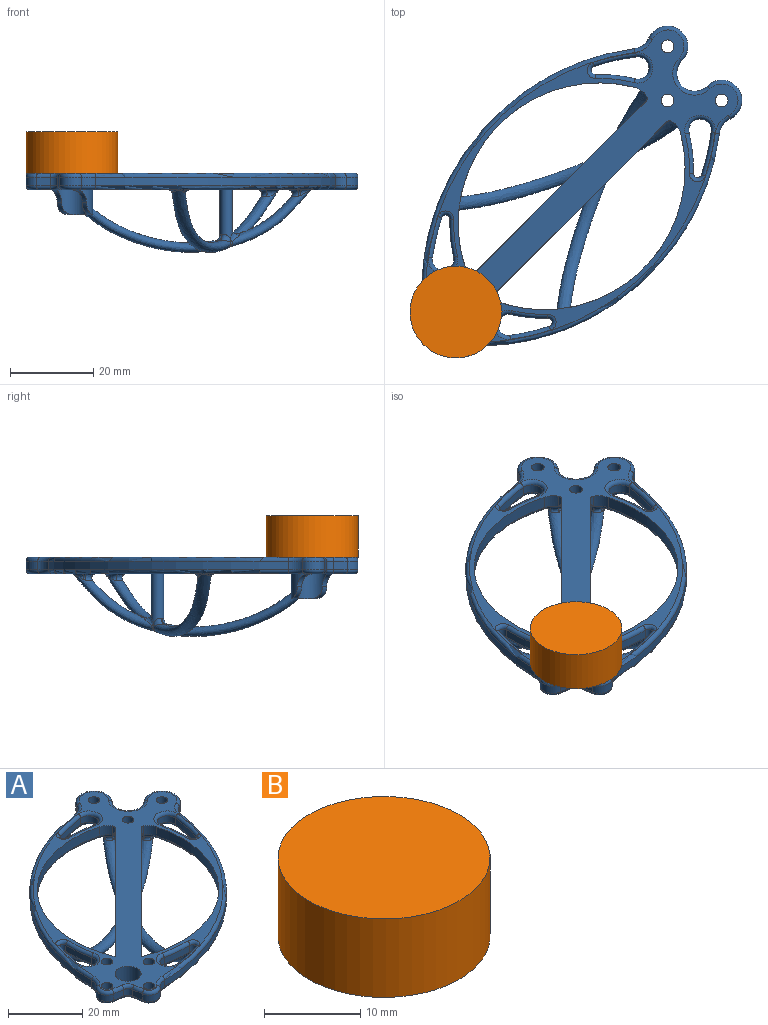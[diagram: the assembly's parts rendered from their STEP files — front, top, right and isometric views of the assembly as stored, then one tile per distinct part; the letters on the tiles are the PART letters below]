
ASSEMBLY  parts=2 mates=1
PART A: 190 faces, bbox 82.3x82.3x19.1 mm
  f0: plane 35.32x35.1mm, normal (0,0,-1), area 158.4mm2, adj f44,f45,f46,f47,f56,f72,f73,f75
  f1: bspline ~3.8x3.75mm, area 3mm2, adj f3,f5,f16,f170
  f2: bspline ~5.97x4.34mm, area 4.7mm2, adj f4,f5,f17,f173
  f3: bspline ~21.16x13.88mm, area 178.6mm2, adj f1,f7,f15,f16,f142,f143,f144,f145
  f4: bspline ~40.35x14.86mm, area 345.9mm2, adj f2,f6,f14,f17,f124,f125,f126,f127
  f5: bspline ~60.31x25.47mm, area 536.7mm2, adj f1,f2,f6,f7,f14,f15,f16,f17
  f6: bspline ~3.46x3.45mm, area 3.1mm2, adj f4,f5,f14,f176
  f7: bspline ~6.58x4.81mm, area 6.2mm2, adj f3,f5,f15,f179
  f8: cylinder r=4.5mm len=3.73mm, axis (0,0,1), area 11mm2, adj f9,f13,f57,f110,f157,f158
  f9: cylinder r=33.94mm len=49.02mm, axis (0,0,1), area 230.7mm2, adj f8,f10,f57,f112,f149,f151,f164
  f10: cylinder r=4.5mm len=2.03mm, axis (0,0,1), area 0.1mm2, adj f9,f11,f114,f152
  f11: cylinder r=33.94mm len=49.02mm, axis (0,0,1), area 230.7mm2, adj f10,f12,f57,f115,f150,f153,f159
  f12: cylinder r=4.5mm len=3.73mm, axis (0,0,1), area 11mm2, adj f11,f13,f57,f113,f154,f155
  f13: cylinder r=4.5mm len=3.84mm, axis (0,0,1), area 0.3mm2, adj f8,f12,f111,f156
  f14: bspline ~2.25x2.25mm, area 1.8mm2, adj f4,f5,f6,f17
  f15: bspline ~3x2.99mm, area 2.5mm2, adj f3,f5,f7,f16
  f16: bspline ~2.93x2.91mm, area 2.5mm2, adj f1,f3,f5,f15
  f17: bspline ~2.22x2.22mm, area 1.7mm2, adj f2,f4,f5,f14
  f18: plane 70.48x70.39mm, normal (0,0,-1), area 284.4mm2, adj f50,f51,f52,f72,f74,f76,f78,f80
  f19: cylinder r=2.59mm len=5.17mm, axis (0,0,1), area 19.1mm2, adj f20,f48,f86,f102
  f20: cylinder r=35.94mm len=9.11mm, axis (0,0,1), area 19.3mm2, adj f19,f21,f88,f104
  f21: cylinder r=1mm len=2.1mm, axis (0,0,1), area 6mm2, adj f20,f48,f89,f105
  f22: cylinder r=2.56mm len=5.12mm, axis (0,0,1), area 18.9mm2, adj f23,f49,f92,f106
  f23: cylinder r=56.93mm len=9.47mm, axis (0,0,1), area 20.4mm2, adj f22,f24,f90,f108
  f24: cylinder r=1mm len=2.1mm, axis (0,0,1), area 6mm2, adj f23,f49,f91,f109
  f25: cylinder r=35.97mm len=9.55mm, axis (0,0,1), area 20.2mm2, adj f26,f53,f94,f117
  f26: cylinder r=2.69mm len=5.38mm, axis (0,0,1), area 19.8mm2, adj f25,f27,f96,f116
  f27: cylinder r=56.93mm len=10.18mm, axis (0,0,1), area 22mm2, adj f26,f53,f97,f118
  f28: cylinder r=2.72mm len=5.43mm, axis (0,0,1), area 20mm2, adj f29,f54,f99,f120
  f29: cylinder r=35.94mm len=9.74mm, axis (0,0,1), area 20.6mm2, adj f28,f30,f101,f122
  f30: cylinder r=1mm len=2.1mm, axis (0,0,1), area 6mm2, adj f29,f54,f100,f123
  f31: cylinder r=4.5mm len=3.49mm, axis (0,0,1), area 9.5mm2, adj f32,f55,f59,f82
  f32: cylinder r=58.96mm len=57.62mm, axis (0,0,1), area 176.3mm2, adj f31,f33,f58,f84
  f33: cylinder r=4.5mm len=3.44mm, axis (0,0,1), area 8.3mm2, adj f32,f34,f60,f85
  f34: cylinder r=3mm len=5.31mm, axis (0,0,1), area 14.6mm2, adj f33,f35,f62,f83
  f35: plane 3.28x2.1mm, normal (-0.99,-0.14,0), area 7mm2, adj f34,f36,f64,f81
  f36: cylinder r=2mm len=2.1mm, axis (0,0,1), area 5.4mm2, adj f35,f37,f66,f79
  f37: plane 3.28x2.1mm, normal (-0.14,-0.99,0), area 7mm2, adj f36,f38,f68,f77
  f38: cylinder r=3mm len=5.31mm, axis (0,0,1), area 14.6mm2, adj f37,f39,f70,f75
  f39: cylinder r=4.5mm len=3.44mm, axis (0,0,1), area 8.3mm2, adj f38,f40,f71,f73
  f40: cylinder r=58.96mm len=57.62mm, axis (0,0,1), area 176.3mm2, adj f39,f41,f69,f72
  f41: cylinder r=4.5mm len=3.49mm, axis (0,0,1), area 9.5mm2, adj f40,f42,f67,f74
  f42: cylinder r=4.91mm len=9.37mm, axis (0,0,1), area 36mm2, adj f41,f43,f65,f76
  f43: cylinder r=4.28mm len=7.31mm, axis (0,0,1), area 28.3mm2, adj f42,f55,f63,f78
  f44: cylinder r=1.55mm len=4mm, axis (0,0,1), area 39mm2, adj f0,f57
  f45: cylinder r=1.55mm len=4mm, axis (0,0,1), area 39mm2, adj f0,f57
  f46: cylinder r=1.55mm len=4mm, axis (0,0,1), area 39mm2, adj f0,f57
  f47: cylinder r=3.5mm len=10mm, axis (0,0,1), area 153.9mm2, adj f0,f57,f185,f186,f187,f188,f189
  f48: cylinder r=56.96mm len=9.66mm, axis (0,0,1), area 20.9mm2, adj f19,f21,f87,f103
  f49: cylinder r=35.97mm len=8.93mm, axis (0,0,1), area 18.9mm2, adj f22,f24,f93,f107
  f50: cylinder r=1.55mm len=4mm, axis (0,0,1), area 39mm2, adj f18,f57
  f51: cylinder r=1.55mm len=4mm, axis (0,0,1), area 39mm2, adj f18,f57
  f52: cylinder r=1.55mm len=4mm, axis (0,0,1), area 39mm2, adj f18,f57
  f53: cylinder r=1mm len=2.1mm, axis (0,0,1), area 6mm2, adj f25,f27,f95,f119
  f54: cylinder r=56.96mm len=10.38mm, axis (0,0,1), area 22.4mm2, adj f28,f30,f98,f121
  f55: cylinder r=4.91mm len=9.37mm, axis (0,0,1), area 36mm2, adj f31,f43,f61,f80
  f56: cylinder r=1.55mm len=4mm, axis (0,0,1), area 39mm2, adj f0,f57
  f57: plane 77.92x77.92mm, normal (0,0,1), area 1135mm2, adj f8,f9,f11,f12,f44,f45,f46,f47
  f58: torus R=58.01mm, axis (0,0,-1), area 124.6mm2, adj f32,f57,f59,f60
  f59: torus R=5.45mm, axis (0,0,-1), area 7.3mm2, adj f31,f57,f58,f61
  f60: torus R=5.45mm, axis (0,0,-1), area 6.4mm2, adj f33,f57,f58,f62
  f61: torus R=3.96mm, axis (0,0,-1), area 23.8mm2, adj f55,f57,f59,f63
  f62: torus R=2.05mm, axis (0,0,-1), area 9.2mm2, adj f34,f57,f60,f64
  f63: torus R=5.23mm, axis (0,0,-1), area 21.7mm2, adj f43,f57,f61,f65
  f64: cylinder r=0.95mm len=3.42mm, axis (-0.14,0.99,0), area 4.9mm2, adj f35,f57,f62,f66
  f65: torus R=3.96mm, axis (0,0,-1), area 23.8mm2, adj f42,f57,f63,f67
  f66: torus R=2.95mm, axis (0,0,-1), area 4.5mm2, adj f36,f57,f64,f68
  f67: torus R=5.45mm, axis (0,0,-1), area 7.3mm2, adj f41,f57,f65,f69
  f68: cylinder r=0.95mm len=3.42mm, axis (-0.99,0.14,0), area 4.9mm2, adj f37,f57,f66,f70
  f69: torus R=58.01mm, axis (0,0,-1), area 124.6mm2, adj f40,f57,f67,f71
  f70: torus R=2.05mm, axis (0,0,-1), area 9.2mm2, adj f38,f57,f68,f71
  f71: torus R=5.45mm, axis (0,0,-1), area 6.4mm2, adj f39,f57,f69,f70
  f72: torus R=58.01mm, axis (0,0,-1), area 124.1mm2, adj f0,f18,f40,f73,f74,f129
  f73: torus R=5.45mm, axis (0,0,-1), area 6.4mm2, adj f0,f39,f72,f75
  f74: torus R=5.45mm, axis (0,0,-1), area 7.3mm2, adj f18,f41,f72,f76
  f75: torus R=2.05mm, axis (0,0,-1), area 9.2mm2, adj f0,f38,f73,f77
  f76: torus R=3.96mm, axis (0,0,-1), area 23.8mm2, adj f18,f42,f74,f78
  f77: cylinder r=0.95mm len=3.42mm, axis (0.99,-0.14,0), area 4.9mm2, adj f0,f37,f75,f79
  f78: torus R=5.23mm, axis (0,0,-1), area 21.7mm2, adj f18,f43,f76,f80
  f79: torus R=2.95mm, axis (0,0,-1), area 4.5mm2, adj f0,f36,f77,f81
  f80: torus R=3.96mm, axis (0,0,-1), area 23.8mm2, adj f18,f55,f78,f82
  f81: cylinder r=0.95mm len=3.42mm, axis (0.14,-0.99,0), area 4.9mm2, adj f0,f35,f79,f83
  f82: torus R=5.45mm, axis (0,0,-1), area 7.3mm2, adj f18,f31,f80,f84
  f83: torus R=2.05mm, axis (0,0,-1), area 9.2mm2, adj f0,f34,f81,f85
  f84: torus R=58.01mm, axis (0,0,-1), area 124.1mm2, adj f0,f18,f32,f82,f85,f138
  f85: torus R=5.45mm, axis (0,0,-1), area 6.4mm2, adj f0,f33,f83,f84
  f86: torus R=3.54mm, axis (0,0,-1), area 15.3mm2, adj f19,f57,f87,f88
  f87: torus R=57.91mm, axis (0,0,-1), area 14.9mm2, adj f48,f57,f86,f89
  f88: torus R=34.99mm, axis (0,0,-1), area 13.6mm2, adj f20,f57,f86,f89
  f89: torus R=1.95mm, axis (0,0,-1), area 5.7mm2, adj f21,f57,f87,f88
  f90: torus R=57.88mm, axis (0,0,-1), area 14.6mm2, adj f23,f57,f91,f92
  f91: torus R=1.95mm, axis (0,0,-1), area 5.7mm2, adj f24,f57,f90,f93
  f92: torus R=3.51mm, axis (0,0,-1), area 15.2mm2, adj f22,f57,f90,f93
  f93: torus R=35.02mm, axis (0,0,-1), area 13.3mm2, adj f49,f57,f91,f92
  f94: torus R=35.02mm, axis (0,0,-1), area 14.2mm2, adj f25,f57,f95,f96
  f95: torus R=1.95mm, axis (0,0,-1), area 5.7mm2, adj f53,f57,f94,f97
  f96: torus R=3.64mm, axis (0,0,-1), area 15.9mm2, adj f26,f57,f94,f97
  f97: torus R=57.88mm, axis (0,0,-1), area 15.7mm2, adj f27,f57,f95,f96
  f98: torus R=57.91mm, axis (0,0,-1), area 16mm2, adj f54,f57,f99,f100
  f99: torus R=3.67mm, axis (0,0,-1), area 16mm2, adj f28,f57,f98,f101
  f100: torus R=1.95mm, axis (0,0,-1), area 5.7mm2, adj f30,f57,f98,f101
  f101: torus R=34.99mm, axis (0,0,-1), area 14.5mm2, adj f29,f57,f99,f100
  f102: torus R=3.54mm, axis (0,0,-1), area 15.3mm2, adj f0,f19,f103,f104
  f103: torus R=57.91mm, axis (0,0,-1), area 14.9mm2, adj f0,f48,f102,f105
  f104: torus R=34.99mm, axis (0,0,-1), area 13.6mm2, adj f0,f20,f102,f105
  f105: torus R=1.95mm, axis (0,0,-1), area 5.1mm2, adj f0,f21,f103,f104,f126
  f106: torus R=3.51mm, axis (0,0,-1), area 15.2mm2, adj f0,f22,f107,f108
  f107: torus R=35.02mm, axis (0,0,-1), area 13.3mm2, adj f0,f49,f106,f109
  f108: torus R=57.88mm, axis (0,0,-1), area 14.6mm2, adj f0,f23,f106,f109
  f109: torus R=1.95mm, axis (0,0,-1), area 5.1mm2, adj f0,f24,f107,f108,f137
  f110: torus R=5.45mm, axis (0,0,-1), area 7.7mm2, adj f8,f18,f111,f112,f135
  f111: torus R=3.55mm, axis (0,0,-1), area 8mm2, adj f13,f18,f110,f113
  f112: torus R=34.89mm, axis (0,0,-1), area 113.4mm2, adj f0,f9,f18,f110,f114,f125
  f113: torus R=5.45mm, axis (0,0,-1), area 7.7mm2, adj f12,f18,f111,f115,f144
  f114: torus R=5.45mm, axis (0,0,-1), area 4.7mm2, adj f0,f10,f112,f115
  f115: torus R=34.89mm, axis (0,0,-1), area 113.5mm2, adj f0,f11,f18,f113,f114,f141
  f116: torus R=3.64mm, axis (0,0,-1), area 14.6mm2, adj f18,f26,f117,f118,f131
  f117: torus R=35.02mm, axis (0,0,-1), area 14.2mm2, adj f18,f25,f116,f119
  f118: torus R=57.88mm, axis (0,0,-1), area 15.7mm2, adj f18,f27,f116,f119
  f119: torus R=1.95mm, axis (0,0,-1), area 5.7mm2, adj f18,f53,f117,f118
  f120: torus R=3.67mm, axis (0,0,-1), area 14.8mm2, adj f18,f28,f121,f122,f143
  f121: torus R=57.91mm, axis (0,0,-1), area 16mm2, adj f18,f54,f120,f123
  f122: torus R=34.99mm, axis (0,0,-1), area 14.5mm2, adj f18,f29,f120,f123
  f123: torus R=1.95mm, axis (0,0,-1), area 5.7mm2, adj f18,f30,f121,f122
  f124: bspline ~1.4x1.38mm, area 0.5mm2, adj f0,f4,f125,f126
  f125: bspline ~5.08x1.83mm, area 6.8mm2, adj f4,f112,f124,f127
  f126: bspline ~2.8x1.7mm, area 1.9mm2, adj f4,f105,f124,f128
  f127: bspline ~3.95x1.83mm, area 3.8mm2, adj f4,f18,f125,f129
  f128: bspline ~1.47x1.28mm, area 0.7mm2, adj f0,f4,f126,f130
  f129: bspline ~3.56x1.97mm, area 1.8mm2, adj f4,f72,f127,f130
  f130: bspline ~1.08x0.91mm, area 0.1mm2, adj f0,f4,f128,f129
  f131: bspline ~3.18x3.14mm, area 3.5mm2, adj f5,f116,f132,f133
  f132: bspline ~3.64x2.04mm, area 2.3mm2, adj f5,f18,f131,f134
  f133: bspline ~1.93x1.59mm, area 1.4mm2, adj f5,f18,f131,f135
  f134: bspline ~4.99x3.49mm, area 8mm2, adj f5,f18,f132,f135
  f135: bspline ~2.68x2.64mm, area 4.7mm2, adj f5,f110,f133,f134
  f136: bspline ~1.95x1.6mm, area 0.8mm2, adj f0,f5,f137,f138
  f137: bspline ~2.81x1.68mm, area 1.9mm2, adj f5,f109,f136,f139
  f138: bspline ~3.59x1.97mm, area 1.8mm2, adj f5,f84,f136,f140
  f139: bspline ~1.48x1.2mm, area 0.6mm2, adj f0,f5,f137,f141
  f140: bspline ~3.77x1.8mm, area 3.9mm2, adj f5,f18,f138,f141
  f141: bspline ~5.11x1.83mm, area 6.8mm2, adj f5,f115,f139,f140
  f142: bspline ~1.93x1.59mm, area 1.4mm2, adj f3,f18,f143,f144
  f143: bspline ~3.14x3.09mm, area 3.5mm2, adj f3,f120,f142,f145
  f144: bspline ~2.68x2.65mm, area 4.7mm2, adj f3,f113,f142,f146
  f145: bspline ~1.91x0.95mm, area 1.2mm2, adj f3,f18,f143,f147
  f146: bspline ~3.55x3.45mm, area 6.6mm2, adj f3,f18,f144,f147
  f147: bspline ~3.73x2.06mm, area 2.5mm2, adj f3,f18,f145,f146
  f148: plane 45.62x45.62mm, normal (0,0,-1), area 322.4mm2, adj f151,f152,f153,f156,f160,f165,f182
  f149: plane 42.57x42.57mm, normal (-0.71,0.71,0), area 90.4mm2, adj f9,f57,f157,f164,f165,f166,f167
  f150: plane 42.57x42.57mm, normal (0.71,-0.71,0), area 90.4mm2, adj f11,f57,f154,f159,f160,f161,f162
  f151: torus R=32.94mm, axis (0,0,1), area 2.7mm2, adj f9,f148,f152,f164
  f152: torus R=3.5mm, axis (0,0,1), area 4.2mm2, adj f10,f148,f151,f153
  f153: torus R=32.94mm, axis (0,0,1), area 2.7mm2, adj f11,f148,f152,f159
  f154: cylinder r=1mm len=3mm, axis (0,0,1), area 3mm2, adj f12,f57,f150,f163
  f155: torus R=3.5mm, axis (0,0,1), area 1mm2, adj f12,f156,f162,f163
  f156: torus R=5.5mm, axis (0,0,1), area 9.8mm2, adj f13,f148,f155,f158,f161,f166
  f157: cylinder r=1mm len=3mm, axis (0,0,1), area 3mm2, adj f8,f57,f149,f168
  f158: torus R=3.5mm, axis (0,0,1), area 1mm2, adj f8,f156,f167,f168
  f159: bspline ~1.66x1.6mm, area 1.1mm2, adj f11,f150,f153,f160
  f160: cylinder r=0.5mm len=41.73mm, axis (-0.71,-0.71,0), area 46mm2, adj f148,f150,f159,f161
  f161: bspline ~1.46x1.2mm, area 0.4mm2, adj f150,f156,f160,f162
  f162: bspline ~0.77x0.6mm, area 0.1mm2, adj f150,f155,f161,f163
  f163: bspline ~1.59x1.35mm, area 0.4mm2, adj f154,f155,f162
  f164: bspline ~1.66x1.6mm, area 1.1mm2, adj f9,f149,f151,f165
  f165: cylinder r=0.5mm len=41.73mm, axis (0.71,0.71,0), area 46mm2, adj f148,f149,f164,f166,f183
  f166: bspline ~1.46x1.2mm, area 0.4mm2, adj f149,f156,f165,f167
  f167: bspline ~0.77x0.64mm, area 0.1mm2, adj f149,f158,f166,f168
  f168: bspline ~1.59x1.35mm, area 0.4mm2, adj f157,f158,f167
  f169: cylinder r=1.5mm len=12.33mm, axis (0,0,1), area 103.4mm2, adj f171,f175,f177,f181,f182,f183
  f170: bspline ~0.56x0.55mm, area 0mm2, adj f1,f3,f171,f172
  f171: bspline ~3.35x3.29mm, area 6.7mm2, adj f5,f169,f170,f172,f174
  f172: bspline ~1.75x1.74mm, area 1mm2, adj f170,f171,f175
  f173: bspline ~0.6x0.5mm, area 0mm2, adj f2,f5,f174,f177
  f174: bspline ~0.72x0.52mm, area 0.1mm2, adj f171,f173,f177
  f175: bspline ~3.28x3.26mm, area 6.6mm2, adj f3,f169,f172,f178
  f176: bspline ~0.6x0.59mm, area 0mm2, adj f5,f6,f177,f180
  f177: bspline ~2.85x1.87mm, area 4.3mm2, adj f4,f169,f173,f174,f176,f180
  f178: bspline ~0.74x0.5mm, area 0.2mm2, adj f175,f179,f181
  f179: bspline ~0.47x0.47mm, area 0mm2, adj f3,f7,f178,f181
  f180: bspline ~1.52x1.05mm, area 0.4mm2, adj f176,f177,f181
  f181: bspline ~2.89x1.85mm, area 4.4mm2, adj f5,f169,f178,f179,f180
  f182: torus R=3mm, axis (0,0,1), area 28.8mm2, adj f148,f169,f183
  f183: bspline ~2.26x2.26mm, area 1.5mm2, adj f165,f169,f182
  f184: cylinder r=5mm len=9.95mm, axis (0,0,1), area 94.2mm2, adj f0,f185,f186,f187,f188,f189
  f185: plane 5.71x5.71mm, normal (0,0,-1), area 10mm2, adj f47,f184,f186,f188
  f186: cylinder r=3mm len=4.38mm, axis (0.71,-0.71,0), area 6.3mm2, adj f47,f184,f185,f187
  f187: cylinder r=3mm len=4.38mm, axis (-0.71,0.71,0), area 6.3mm2, adj f0,f47,f184,f186
  f188: cylinder r=3mm len=4.38mm, axis (0.71,-0.71,0), area 6.3mm2, adj f47,f184,f185,f189
  f189: cylinder r=3mm len=4.38mm, axis (-0.71,0.71,0), area 6.3mm2, adj f0,f47,f184,f188
PART B: 3 faces, bbox 22.1x22.1x10 mm
  f0: cylinder r=11.04mm len=22.07mm, axis (0,0,-1), area 693.3mm2, adj f1,f2
  f1: plane 22.07x22.07mm, normal (0,0,1), area 382.6mm2, adj f0
  f2: plane 22.07x22.07mm, normal (0,0,-1), area 382.6mm2, adj f0
PLACE A t=(-4.31,5.63,-27.21)mm
PLACE B t=(-4.31,5.63,-27.21)mm
MATE fastened A.f47 <-> B.f0  axis (0,0,1) through (-95.22,-69.78,-27.21)mm
